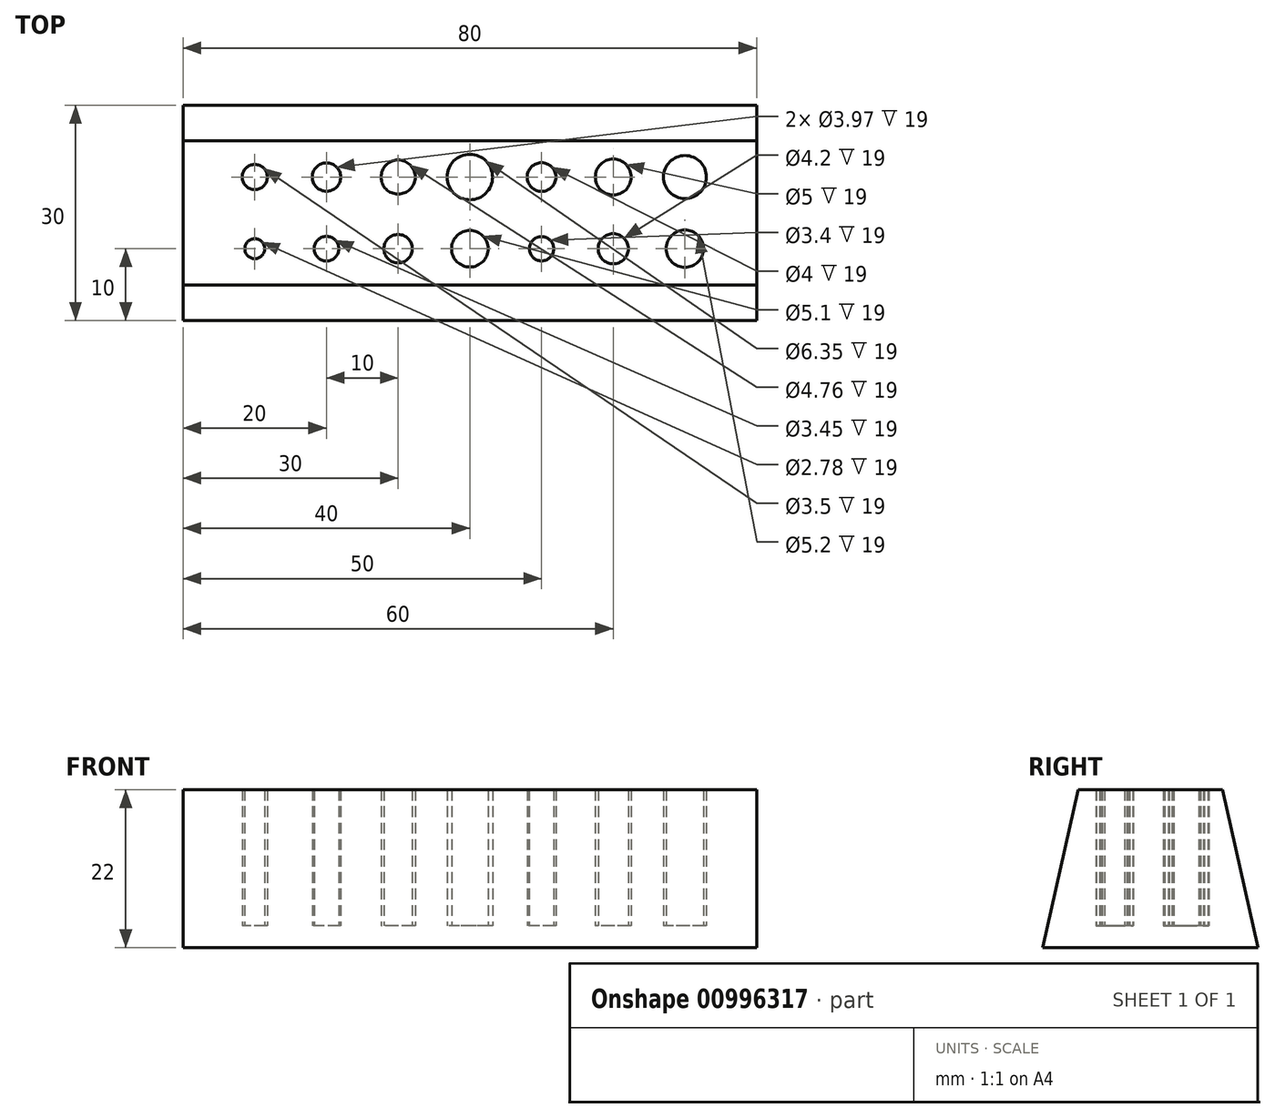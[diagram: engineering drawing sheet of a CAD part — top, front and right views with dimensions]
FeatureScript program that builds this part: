
annotation { "Feature Type Name" : "Feature", "Feature Type Description" : "" }
export const myFeature = defineFeature(function(context is Context, id is Id, definition is map)
    precondition{}
    {
        {
            var Q0;
            Q0=qCreatedBy(makeId("Top.planeOp"),FACE);
            var sketch = newSketch(context, id + "F0", { "sketchPlane" : qUnion([Q0])});
            skLineSegment(sketch, "E0", {"start": v(0, 0) * mm, "end": v(0, 30) * mm});
            skLineSegment(sketch, "E1", {"start": v(80, 20) * mm, "end": v(0, 20) * mm, "construction": true});
            skLineSegment(sketch, "E2", {"start": v(80, 10) * mm, "end": v(0, 10) * mm, "construction": true});
            skLineSegment(sketch, "E3", {"start": v(0, 0) * mm, "end": v(10, 0) * mm});
            skLineSegment(sketch, "E4", {"start": v(10, 0) * mm, "end": v(20, 0) * mm});
            skLineSegment(sketch, "E5", {"start": v(20, 0) * mm, "end": v(30, 0) * mm});
            skLineSegment(sketch, "E6", {"start": v(30, 0) * mm, "end": v(40, 0) * mm});
            skLineSegment(sketch, "E7", {"start": v(40, 0) * mm, "end": v(50, 0) * mm});
            skLineSegment(sketch, "E8", {"start": v(50, 0) * mm, "end": v(60, 0) * mm});
            skLineSegment(sketch, "E9", {"start": v(60, 0) * mm, "end": v(70, 0) * mm});
            skLineSegment(sketch, "E10", {"start": v(70, 0) * mm, "end": v(80, 0) * mm});
            skLineSegment(sketch, "E11", {"start": v(10, 0) * mm, "end": v(10, 30) * mm, "construction": true});
            skLineSegment(sketch, "E12", {"start": v(20, 0) * mm, "end": v(20, 30) * mm, "construction": true});
            skLineSegment(sketch, "E13", {"start": v(30, 0) * mm, "end": v(30, 30) * mm, "construction": true});
            skLineSegment(sketch, "E14", {"start": v(40, 30) * mm, "end": v(40, 0) * mm, "construction": true});
            skLineSegment(sketch, "E15", {"start": v(50, 0) * mm, "end": v(50, 30) * mm, "construction": true});
            skLineSegment(sketch, "E16", {"start": v(70, 30) * mm, "end": v(70, 0) * mm, "construction": true});
            skLineSegment(sketch, "E17", {"start": v(60, 0) * mm, "end": v(60, 30) * mm, "construction": true});
            skCircle(sketch, "E18", {"center": v(10, 20) * mm, "radius": 1.75 * mm});
            skCircle(sketch, "E19", {"center": v(10, 10) * mm, "radius": 1.39 * mm});
            skCircle(sketch, "E20", {"center": v(20, 20) * mm, "radius": 1.99 * mm});
            skCircle(sketch, "E21", {"center": v(20, 10) * mm, "radius": 1.72 * mm});
            skCircle(sketch, "E22", {"center": v(30, 20) * mm, "radius": 2.38 * mm});
            skCircle(sketch, "E23", {"center": v(30, 10) * mm, "radius": 1.99 * mm});
            skCircle(sketch, "E24", {"center": v(40, 20) * mm, "radius": 3.17 * mm});
            skCircle(sketch, "E25", {"center": v(40, 10) * mm, "radius": 2.55 * mm});
            skCircle(sketch, "E26", {"center": v(50, 20) * mm, "radius": 2 * mm});
            skCircle(sketch, "E27", {"center": v(50, 10) * mm, "radius": 1.7 * mm});
            skCircle(sketch, "E28", {"center": v(60, 20) * mm, "radius": 2.5 * mm});
            skCircle(sketch, "E29", {"center": v(60, 10) * mm, "radius": 2.1 * mm});
            skCircle(sketch, "E30", {"center": v(70, 20) * mm, "radius": 3 * mm});
            skCircle(sketch, "E31", {"center": v(70, 10) * mm, "radius": 2.6 * mm});
            skLineSegment(sketch, "E32", {"start": v(0, 30) * mm, "end": v(80, 30) * mm});
            skLineSegment(sketch, "E33", {"start": v(80, 0) * mm, "end": v(80, 30) * mm});
            skSolve(sketch);
        }
        {
            var Q0;
            Q0=makeQuery(id+"F0.imprint","IMPRINT",FACE,{"disambiguationData":[TD([[makeQuery(id+"F0.imprint","IMPRINT",EDGE,{"derivedFrom":sQuery(id+"F0.wireOp",EDGE,"E0")}),-1.0]])]});
            extrude(context, id + "F1", {"entities" : qUnion([Q0]), "depth" : 22 * mm, "offsetDistance" : 25 * mm});
        }
        {
            var Q0;
            Q0=makeQuery(id+"F0.imprint","IMPRINT",FACE,{"disambiguationData":[TD([[makeQuery(id+"F0.imprint","IMPRINT",EDGE,{"derivedFrom":sQuery(id+"F0.wireOp",EDGE,"E30")}),1.0]])]});
            var Q1;
            Q1=makeQuery(id+"F0.imprint","IMPRINT",FACE,{"disambiguationData":[TD([[makeQuery(id+"F0.imprint","IMPRINT",EDGE,{"derivedFrom":sQuery(id+"F0.wireOp",EDGE,"E31")}),1.0]])]});
            var Q2;
            Q2=makeQuery(id+"F0.imprint","IMPRINT",FACE,{"disambiguationData":[TD([[makeQuery(id+"F0.imprint","IMPRINT",EDGE,{"derivedFrom":sQuery(id+"F0.wireOp",EDGE,"E29")}),1.0]])]});
            var Q3;
            Q3=makeQuery(id+"F0.imprint","IMPRINT",FACE,{"disambiguationData":[TD([[makeQuery(id+"F0.imprint","IMPRINT",EDGE,{"derivedFrom":sQuery(id+"F0.wireOp",EDGE,"E28")}),1.0]])]});
            var Q4;
            Q4=makeQuery(id+"F0.imprint","IMPRINT",FACE,{"disambiguationData":[TD([[makeQuery(id+"F0.imprint","IMPRINT",EDGE,{"derivedFrom":sQuery(id+"F0.wireOp",EDGE,"E26")}),1.0]])]});
            var Q5;
            Q5=makeQuery(id+"F0.imprint","IMPRINT",FACE,{"disambiguationData":[TD([[makeQuery(id+"F0.imprint","IMPRINT",EDGE,{"derivedFrom":sQuery(id+"F0.wireOp",EDGE,"E27")}),1.0]])]});
            var Q6;
            Q6=makeQuery(id+"F0.imprint","IMPRINT",FACE,{"disambiguationData":[TD([[makeQuery(id+"F0.imprint","IMPRINT",EDGE,{"derivedFrom":sQuery(id+"F0.wireOp",EDGE,"E24")}),1.0]])]});
            var Q7;
            Q7=makeQuery(id+"F0.imprint","IMPRINT",FACE,{"disambiguationData":[TD([[makeQuery(id+"F0.imprint","IMPRINT",EDGE,{"derivedFrom":sQuery(id+"F0.wireOp",EDGE,"E25")}),1.0]])]});
            var Q8;
            Q8=makeQuery(id+"F0.imprint","IMPRINT",FACE,{"disambiguationData":[TD([[makeQuery(id+"F0.imprint","IMPRINT",EDGE,{"derivedFrom":sQuery(id+"F0.wireOp",EDGE,"E23")}),1.0]])]});
            var Q9;
            Q9=makeQuery(id+"F0.imprint","IMPRINT",FACE,{"disambiguationData":[TD([[makeQuery(id+"F0.imprint","IMPRINT",EDGE,{"derivedFrom":sQuery(id+"F0.wireOp",EDGE,"E22")}),1.0]])]});
            var Q10;
            Q10=makeQuery(id+"F0.imprint","IMPRINT",FACE,{"disambiguationData":[TD([[makeQuery(id+"F0.imprint","IMPRINT",EDGE,{"derivedFrom":sQuery(id+"F0.wireOp",EDGE,"E20")}),1.0]])]});
            var Q11;
            Q11=makeQuery(id+"F0.imprint","IMPRINT",FACE,{"disambiguationData":[TD([[makeQuery(id+"F0.imprint","IMPRINT",EDGE,{"derivedFrom":sQuery(id+"F0.wireOp",EDGE,"E21")}),1.0]])]});
            var Q12;
            Q12=makeQuery(id+"F0.imprint","IMPRINT",FACE,{"disambiguationData":[TD([[makeQuery(id+"F0.imprint","IMPRINT",EDGE,{"derivedFrom":sQuery(id+"F0.wireOp",EDGE,"E18")}),1.0]])]});
            var Q13;
            Q13=makeQuery(id+"F0.imprint","IMPRINT",FACE,{"disambiguationData":[TD([[makeQuery(id+"F0.imprint","IMPRINT",EDGE,{"derivedFrom":sQuery(id+"F0.wireOp",EDGE,"E19")}),1.0]])]});
            extrude(context, id + "F2", {"entities" : qUnion([Q0, Q1, Q2, Q3, Q4, Q5, Q6, Q7, Q8, Q9, Q10, Q11, Q12, Q13]), "operationType" : NewBodyOperationType.ADD, "depth" : 3 * mm, "offsetDistance" : 25 * mm});
        }
        {
            var Q0;
            Q0=makeQuery(id+"F1.opExtrude","SWEPT_FACE",FACE,{"disambiguationData":[OSD([sQuery(id+"F0.wireOp",EDGE,"E0")])]});
            var sketch = newSketch(context, id + "F3", { "sketchPlane" : qUnion([Q0])});
            skLineSegment(sketch, "E34", {"start": v(-30, 0) * mm, "end": v(-25.07, 22) * mm});
            skLineSegment(sketch, "E35.MirrorCS", {"start": v(0, 0) * mm, "end": v(-4.93, 22) * mm});
            skSolve(sketch);
        }
        {
            var Q0;
            {var subQ0=sQuery(id+"F3.wireOp",EDGE,"E34");Q0=makeQuery(id+"F3.imprint","IMPRINT",FACE,{"disambiguationData":[TD([[makeQuery(id+"F3.imprint","IMPRINT",EDGE,{"derivedFrom":subQ0}),1.0]])]});}
            var Q1;
            {var subQ0=sQuery(id+"F3.wireOp",EDGE,"E35.MirrorCS");Q1=makeQuery(id+"F3.imprint","IMPRINT",FACE,{"disambiguationData":[TD([[makeQuery(id+"F3.imprint","IMPRINT",EDGE,{"derivedFrom":subQ0}),-1.0]])]});}
            extrude(context, id + "F4", {"entities" : qUnion([Q0, Q1]), "operationType" : NewBodyOperationType.REMOVE, "oppositeDirection" : true, "depth" : 300 * mm, "offsetDistance" : 25 * mm});
        }
    });
